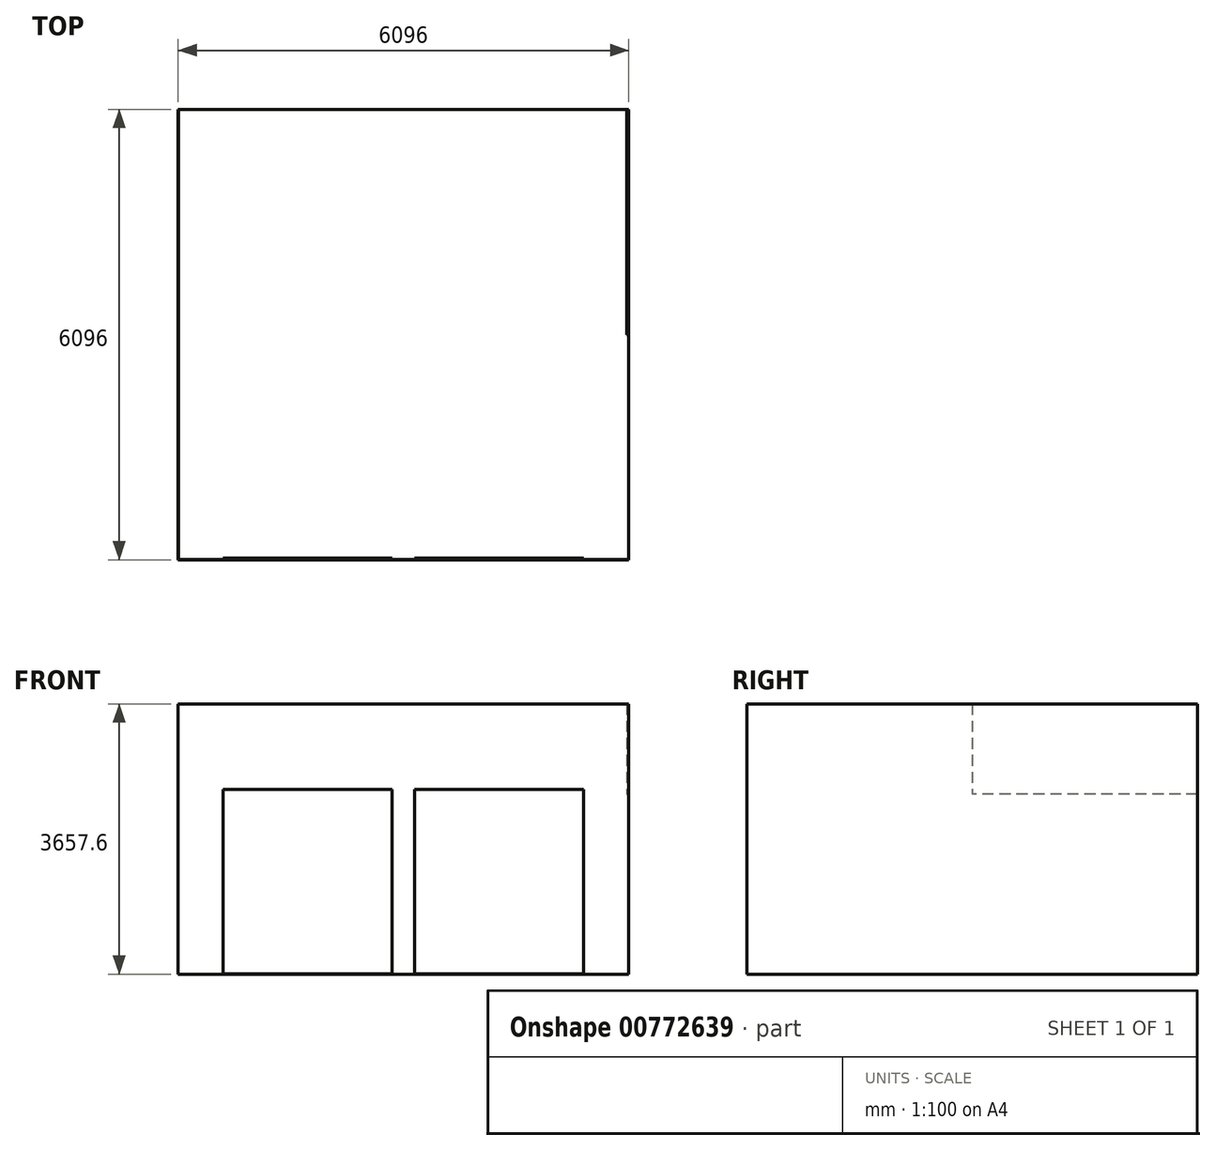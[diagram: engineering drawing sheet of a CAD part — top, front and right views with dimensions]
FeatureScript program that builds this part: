
annotation { "Feature Type Name" : "Feature", "Feature Type Description" : "" }
export const myFeature = defineFeature(function(context is Context, id is Id, definition is map)
    precondition{}
    {
        {
            var Q0;
            Q0=qCreatedBy(makeId("Top.planeOp"),FACE);
            var sketch = newSketch(context, id + "F0", { "sketchPlane" : qUnion([Q0])});
            skLineSegment(sketch, "E0.bottom", {"start": v(0, 0) * mm, "end": v(6096, 0) * mm});
            skLineSegment(sketch, "E0.top", {"start": v(0, 6096) * mm, "end": v(6096, 6096) * mm});
            skLineSegment(sketch, "E0.left", {"start": v(0, 0) * mm, "end": v(0, 6096) * mm});
            skLineSegment(sketch, "E0.right", {"start": v(6096, 0) * mm, "end": v(6096, 6096) * mm});
            skSolve(sketch);
        }
        {
            var Q0;
            Q0=makeQuery(id+"F0.imprint","IMPRINT",FACE,{"disambiguationData":[TD([[makeQuery(id+"F0.imprint","IMPRINT",EDGE,{"derivedFrom":sQuery(id+"F0.wireOp",EDGE,"E0.bottom")}),1.0]])]});
            extrude(context, id + "F1", {"entities" : qUnion([Q0]), "depth" : 3657.6 * mm, "offsetDistance" : 25.4 * mm});
        }
        {
            var Q0;
            Q0=makeQuery(id+"F1.opExtrude","CAP_FACE",FACE,{"disambiguationData":[OSD([sQuery(id+"F0.wireOp",EDGE,"E0.bottom"),sQuery(id+"F0.wireOp",EDGE,"E0.top"),sQuery(id+"F0.wireOp",EDGE,"E0.left"),sQuery(id+"F0.wireOp",EDGE,"E0.right")])],"isStart":false});
            shell(context, id + "F2", {"entities" : qUnion([Q0]), "thickness" : 2.54 * mm});
        }
        {
            var Q0;
            Q0=makeQuery(id+"F1.opExtrude","SWEPT_FACE",FACE,{"disambiguationData":[OSD([sQuery(id+"F0.wireOp",EDGE,"E0.bottom")])]});
            var sketch = newSketch(context, id + "F3", { "sketchPlane" : qUnion([Q0])});
            skLineSegment(sketch, "E1.bottom", {"start": v(609.6, 0) * mm, "end": v(2895.6, 0) * mm});
            skLineSegment(sketch, "E1.top", {"start": v(609.6, 2496.53) * mm, "end": v(2895.6, 2496.53) * mm});
            skLineSegment(sketch, "E1.left", {"start": v(609.6, 0) * mm, "end": v(609.6, 2496.53) * mm});
            skLineSegment(sketch, "E1.right", {"start": v(2895.6, 0) * mm, "end": v(2895.6, 2496.53) * mm});
            skPoint(sketch, "E2.oppositeSnap0", {"position": v(1752.6, 2496.53) * mm});
            skLineSegment(sketch, "E2.bottom", {"start": v(3200.4, 0) * mm, "end": v(5486.4, 0) * mm});
            skLineSegment(sketch, "E2.top", {"start": v(3200.4, 2496.53) * mm, "end": v(5486.4, 2496.53) * mm});
            skLineSegment(sketch, "E2.left", {"start": v(3200.4, 0) * mm, "end": v(3200.4, 2496.53) * mm});
            skLineSegment(sketch, "E2.right", {"start": v(5486.4, 0) * mm, "end": v(5486.4, 2496.53) * mm});
            skSolve(sketch);
        }
        {
            var Q0;
            Q0=makeQuery(id+"F3.imprint","IMPRINT",FACE,{"disambiguationData":[TD([[makeQuery(id+"F3.imprint","IMPRINT",EDGE,{"derivedFrom":sQuery(id+"F3.wireOp",EDGE,"E1.bottom")}),1.0]])]});
            var Q1;
            Q1=makeQuery(id+"F3.imprint","IMPRINT",FACE,{"disambiguationData":[TD([[makeQuery(id+"F3.imprint","IMPRINT",EDGE,{"derivedFrom":sQuery(id+"F3.wireOp",EDGE,"E2.bottom")}),1.0]])]});
            extrude(context, id + "F4", {"entities" : qUnion([Q0, Q1]), "operationType" : NewBodyOperationType.REMOVE, "oppositeDirection" : true, "depth" : 25.4 * mm, "offsetDistance" : 25.4 * mm});
        }
        {
            var Q0;
            Q0=makeQuery(id+"F2.opShell","OFFSET_FACE",FACE,{"disambiguationData":[OSD([sQuery(id+"F0.wireOp",EDGE,"E0.right")])]});
            var sketch = newSketch(context, id + "F5", { "sketchPlane" : qUnion([Q0])});
            skLineSegment(sketch, "E3.bottom", {"start": v(-6093.46, 3657.6) * mm, "end": v(-3045.46, 3657.6) * mm});
            skLineSegment(sketch, "E3.top", {"start": v(-6093.46, 2438.4) * mm, "end": v(-3045.46, 2438.4) * mm});
            skLineSegment(sketch, "E3.left", {"start": v(-6093.46, 3657.6) * mm, "end": v(-6093.46, 2438.4) * mm});
            skLineSegment(sketch, "E3.right", {"start": v(-3045.46, 3657.6) * mm, "end": v(-3045.46, 2438.4) * mm});
            skSolve(sketch);
        }
        {
            var Q0;
            Q0=makeQuery(id+"F5.imprint","IMPRINT",FACE,{"disambiguationData":[TD([[makeQuery(id+"F5.imprint","IMPRINT",EDGE,{"derivedFrom":sQuery(id+"F5.wireOp",EDGE,"E3.bottom")}),1.0]])]});
            extrude(context, id + "F6", {"entities" : qUnion([Q0]), "operationType" : NewBodyOperationType.ADD, "depth" : 25.4 * mm, "offsetDistance" : 25.4 * mm});
        }
    });
